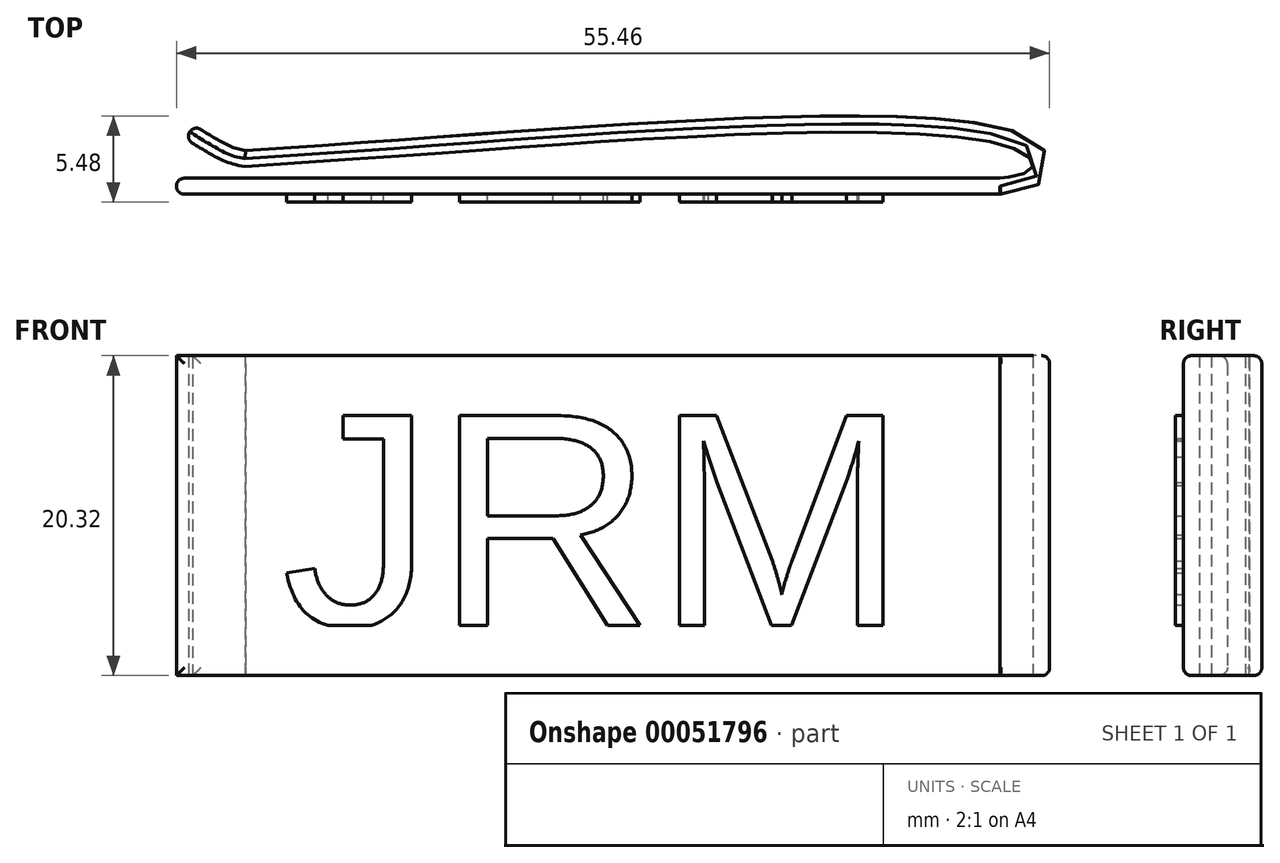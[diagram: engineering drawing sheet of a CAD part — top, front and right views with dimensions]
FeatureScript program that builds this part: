
annotation { "Feature Type Name" : "Feature", "Feature Type Description" : "" }
export const myFeature = defineFeature(function(context is Context, id is Id, definition is map)
    precondition{}
    {
        {
            var Q0;
            Q0=qCreatedBy(makeId("Top.planeOp"),FACE);
            var sketch = newSketch(context, id + "F4", { "sketchPlane" : qUnion([Q0])});
            skLineSegment(sketch, "E0", {"start": v(0, 0) * mm, "end": v(-27.94, 0) * mm});
            skLineSegment(sketch, "E1.MirrorCS", {"start": v(0, 0) * mm, "end": v(24.24, 0) * mm});
            skFitSpline(sketch, "E2", {"points": [v(-23.72, 0.75) * mm, v(-25.79, 1.48) * mm, v(-27.35, 2.43) * mm], "startDerivative": vector(-5.38, 0.65) * mm, "endDerivative": vector(-3.11, 2.13) * mm});
            skFitSpline(sketch, "E3", {"points": [v(24.24, 0) * mm, v(26.2, 0.54) * mm, v(25.17, 1.86) * mm, v(2.48, 2.53) * mm, v(-23.72, 0.75) * mm], "startDerivative": vector(1.69, 0) * mm, "endDerivative": vector(-87.3, -5.57) * mm});
            skFitSpline(sketch, "E4.0", {"points": [v(-23.6, 1.76) * mm, v(-23.78, 1.78) * mm, v(-24.1, 1.84) * mm, v(-24.5, 1.97) * mm, v(-24.85, 2.12) * mm, v(-25.15, 2.29) * mm, v(-25.42, 2.44) * mm, v(-25.7, 2.59) * mm, v(-26.03, 2.78) * mm, v(-26.41, 3.02) * mm, v(-26.66, 3.18) * mm, v(-26.78, 3.26) * mm]});
            skFitSpline(sketch, "E4.1", {"points": [v(24.24, -1.02) * mm, v(24.27, -1.02) * mm, v(24.3, -1.01) * mm, v(24.32, -1.01) * mm, v(24.34, -1.01) * mm, v(24.36, -1) * mm, v(24.4, -1) * mm, v(24.44, -1) * mm, v(24.5, -1) * mm, v(24.58, -0.99) * mm, v(24.7, -0.97) * mm, v(24.85, -0.95) * mm, v(25.03, -0.92) * mm, v(25.23, -0.88) * mm, v(25.5, -0.83) * mm, v(25.86, -0.74) * mm, v(26.23, -0.61) * mm, v(26.53, -0.47) * mm, v(26.76, -0.33) * mm, v(27, -0.12) * mm, v(27.22, 0.18) * mm, v(27.36, 0.55) * mm, v(27.38, 0.94) * mm, v(27.3, 1.28) * mm, v(27.18, 1.57) * mm, v(27.02, 1.8) * mm, v(26.78, 2.06) * mm, v(26.45, 2.33) * mm, v(26, 2.6) * mm, v(25.47, 2.84) * mm, v(24.9, 3.04) * mm, v(24.06, 3.27) * mm, v(22.88, 3.5) * mm, v(21.26, 3.7) * mm, v(19.46, 3.83) * mm, v(17.52, 3.92) * mm, v(15.45, 3.95) * mm, v(12.58, 3.95) * mm, v(9.6, 3.87) * mm, v(6.66, 3.76) * mm, v(4.5, 3.65) * mm, v(2.4, 3.54) * mm, v(0.43, 3.43) * mm, v(-1.45, 3.32) * mm, v(-3.88, 3.16) * mm, v(-6.83, 2.96) * mm, v(-10.43, 2.7) * mm, v(-15.58, 2.32) * mm, v(-20.15, 2) * mm, v(-23.78, 1.77) * mm]});
            skLineSegment(sketch, "E4.2", {"start": v(0, -1.02) * mm, "end": v(24.24, -1.02) * mm});
            skLineSegment(sketch, "E4.3", {"start": v(0, -1.02) * mm, "end": v(-27.94, -1.02) * mm});
            skLineSegment(sketch, "E5", {"start": v(-27.35, 2.43) * mm, "end": v(-27.27, 3) * mm});
            skLineSegment(sketch, "E6", {"start": v(-27.27, 3) * mm, "end": v(-26.78, 3.26) * mm});
            skLineSegment(sketch, "E7", {"start": v(-27.94, 0) * mm, "end": v(-28.27, -1.02) * mm});
            skLineSegment(sketch, "E8", {"start": v(-28.27, -1.02) * mm, "end": v(-27.94, -1.02) * mm});
            skSolve(sketch);
        }
        {
            var Q0;
            Q0 = qSketchRegion(id + "F4", true);
            extrude(context, id + "F0", {"entities" : qUnion([Q0]), "depth" : 20.32 * mm});
        }
        {
            var Q0;
            Q0=makeQuery(id+"F0.opExtrude","SWEPT_EDGE",EDGE,{"disambiguationData":[OSD([sQuery(id+"F4.wireOp",EDGE,"E5"),sQuery(id+"F4.wireOp",EDGE,"E6")])]});
            var Q1;
            Q1=makeQuery(id+"F0.opExtrude","CAP_EDGE",EDGE,{"disambiguationData":[OSD([sQuery(id+"F4.wireOp",EDGE,"E4.0")])],"isStart":false});
            var Q2;
            Q2=makeQuery(id+"F0.opExtrude","CAP_EDGE",EDGE,{"disambiguationData":[OSD([sQuery(id+"F4.wireOp",EDGE,"E4.1")])],"isStart":false});
            var Q3;
            Q3=makeQuery(id+"F0.opExtrude","CAP_EDGE",EDGE,{"disambiguationData":[OSD([sQuery(id+"F4.wireOp",EDGE,"E4.0")])],"isStart":true});
            var Q4;
            Q4=makeQuery(id+"F0.opExtrude","CAP_EDGE",EDGE,{"disambiguationData":[OSD([sQuery(id+"F4.wireOp",EDGE,"E4.1")])],"isStart":true});
            var Q5;
            Q5=makeQuery(id+"F0.opExtrude","CAP_EDGE",EDGE,{"disambiguationData":[OSD([sQuery(id+"F4.wireOp",EDGE,"E4.2"),sQuery(id+"F4.wireOp",EDGE,"E4.3"),sQuery(id+"F4.wireOp",EDGE,"E8")])],"isStart":false});
            var Q6;
            Q6=makeQuery(id+"F0.opExtrude","SWEPT_EDGE",EDGE,{"disambiguationData":[OSD([sQuery(id+"F4.wireOp",EDGE,"E7"),sQuery(id+"F4.wireOp",EDGE,"E8")])]});
            var Q7;
            Q7=makeQuery(id+"F0.opExtrude","CAP_EDGE",EDGE,{"disambiguationData":[OSD([sQuery(id+"F4.wireOp",EDGE,"E4.2"),sQuery(id+"F4.wireOp",EDGE,"E4.3"),sQuery(id+"F4.wireOp",EDGE,"E8")])],"isStart":true});
            var Q8;
            Q8=makeQuery(id+"F0.opExtrude","SWEPT_EDGE",EDGE,{"disambiguationData":[OSD([sQuery(id+"F4.wireOp",EDGE,"E2"),sQuery(id+"F4.wireOp",EDGE,"E5")])]});
            var Q9;
            Q9=makeQuery(id+"F0.opExtrude","SWEPT_EDGE",EDGE,{"disambiguationData":[OSD([sQuery(id+"F4.wireOp",EDGE,"E0"),sQuery(id+"F4.wireOp",EDGE,"E7")])]});
            var Q10;
            Q10=makeQuery(id+"F0.opExtrude","SWEPT_EDGE",EDGE,{"disambiguationData":[OSD([sQuery(id+"F4.wireOp",EDGE,"E4.0"),sQuery(id+"F4.wireOp",EDGE,"E6")])]});
            fillet(context, id + "F1", {"entities" : qUnion([Q0, Q1, Q2, Q3, Q4, Q5, Q6, Q7, Q8, Q9, Q10]), "radius" : 0.5 * mm, "tangentPropagation" : true, "allowEdgeOverflow" : false});
        }
        {
            var Q0;
            Q0=makeQuery(id+"F0.opExtrude","SWEPT_FACE",FACE,{"disambiguationData":[OSD([sQuery(id+"F4.wireOp",EDGE,"E4.2"),sQuery(id+"F4.wireOp",EDGE,"E4.3"),sQuery(id+"F4.wireOp",EDGE,"E8")])]});
            var sketch = newSketch(context, id + "F2", { "sketchPlane" : qUnion([Q0])});
            skPoint(sketch, "E9.rect.middle.positionSnap0", {"position": v(-27.57, 10.16) * mm});
            skPoint(sketch, "E9.rect.centerSnap0", {"position": v(-27.57, 10.16) * mm});
            skLineSegment(sketch, "E10.rect.bottom", {"start": v(-21.37, 3.2) * mm, "end": v(16.82, 3.2) * mm});
            skLineSegment(sketch, "E10.rect.top", {"start": v(-21.37, 17.13) * mm, "end": v(16.82, 17.13) * mm});
            skLineSegment(sketch, "E10.rect.left", {"start": v(-21.37, 3.2) * mm, "end": v(-21.37, 17.13) * mm});
            skLineSegment(sketch, "E10.rect.right", {"start": v(16.82, 3.2) * mm, "end": v(16.82, 17.13) * mm});
            skPoint(sketch, "E10.rect.middle", {"position": v(-2.28, 10.16) * mm});
            skText(sketch, "E11", { "text": "JRM", "fontName": "Arimo-Regular.ttf"});
            const initialGuessF2  = {"E11": [-0.02137, 0.0032, 1, 0, 0.01393]};
            skSetInitialGuess(sketch, initialGuessF2);
            skSolve(sketch);
        }
        {
            var Q0;
            {var subQ5=sQuery(id+"F2.wireOp",EDGE,"E11.sketch_text.stroke-1");Q0=makeQuery(id+"F2.imprint","IMPRINT",FACE,{"disambiguationData":[TD([[makeQuery(id+"F2.imprint","IMPRINT",EDGE,{"derivedFrom":subQ5}),-1.0]])]});}
            var Q1;
            Q1=makeQuery(id+"F2.imprint","IMPRINT",FACE,{"disambiguationData":[TD([[makeQuery(id+"F2.imprint","IMPRINT",EDGE,{"derivedFrom":sQuery(id+"F2.wireOp",EDGE,"E11.sketch_text.stroke-13")}),-1.0]])]});
            var Q2;
            Q2=makeQuery(id+"F2.imprint","IMPRINT",FACE,{"disambiguationData":[TD([[makeQuery(id+"F2.imprint","IMPRINT",EDGE,{"derivedFrom":sQuery(id+"F2.wireOp",EDGE,"E11.sketch_text.stroke-32")}),-1.0]])]});
            extrude(context, id + "F3", {"entities" : qUnion([Q0, Q1, Q2]), "operationType" : NewBodyOperationType.ADD, "depth" : 0.5 * mm});
        }
    });
